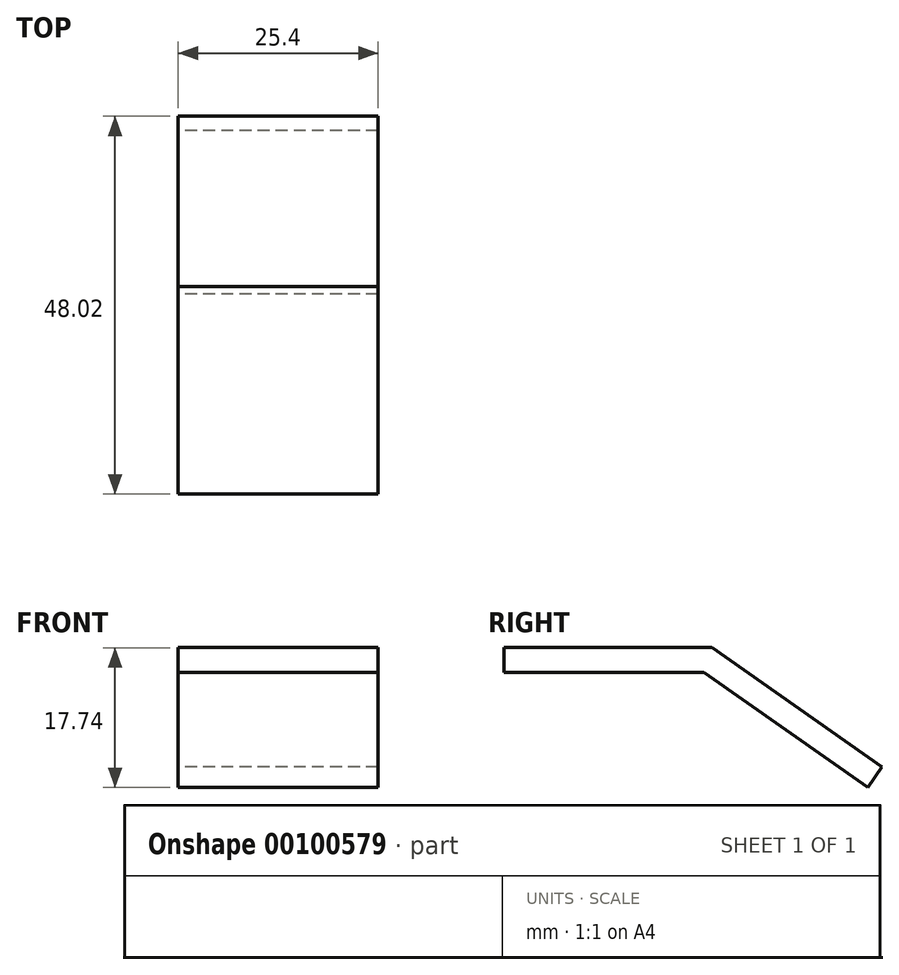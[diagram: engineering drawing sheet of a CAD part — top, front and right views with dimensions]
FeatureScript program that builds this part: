
annotation { "Feature Type Name" : "Feature", "Feature Type Description" : "" }
export const myFeature = defineFeature(function(context is Context, id is Id, definition is map)
    precondition{}
    {
        {
            var Q0;
            Q0=qCreatedBy(makeId("Right.planeOp"),FACE);
            var sketch = newSketch(context, id + "F0", { "sketchPlane" : qUnion([Q0])});
            skLineSegment(sketch, "E0", {"start": v(-14.51, 0) * mm, "end": v(10.89, 0) * mm});
            skLineSegment(sketch, "E1", {"start": v(10.89, 0) * mm, "end": v(31.7, -14.57) * mm});
            skLineSegment(sketch, "E2", {"start": v(31.7, -14.57) * mm, "end": v(33.51, -11.97) * mm});
            skLineSegment(sketch, "E3", {"start": v(33.51, -11.97) * mm, "end": v(11.89, 3.17) * mm});
            skLineSegment(sketch, "E4", {"start": v(11.89, 3.18) * mm, "end": v(-14.51, 3.18) * mm});
            skLineSegment(sketch, "E5", {"start": v(-14.51, 3.18) * mm, "end": v(-14.51, 0) * mm});
            skSolve(sketch);
        }
        {
            var Q0;
            Q0=makeQuery(id+"F0.imprint","IMPRINT",FACE,{"disambiguationData":[TD([[makeQuery(id+"F0.imprint","IMPRINT",EDGE,{"derivedFrom":sQuery(id+"F0.wireOp",EDGE,"E0")}),1.0]])]});
            extrude(context, id + "F1", {"entities" : qUnion([Q0]), "depth" : 25.4 * mm});
        }
    });
